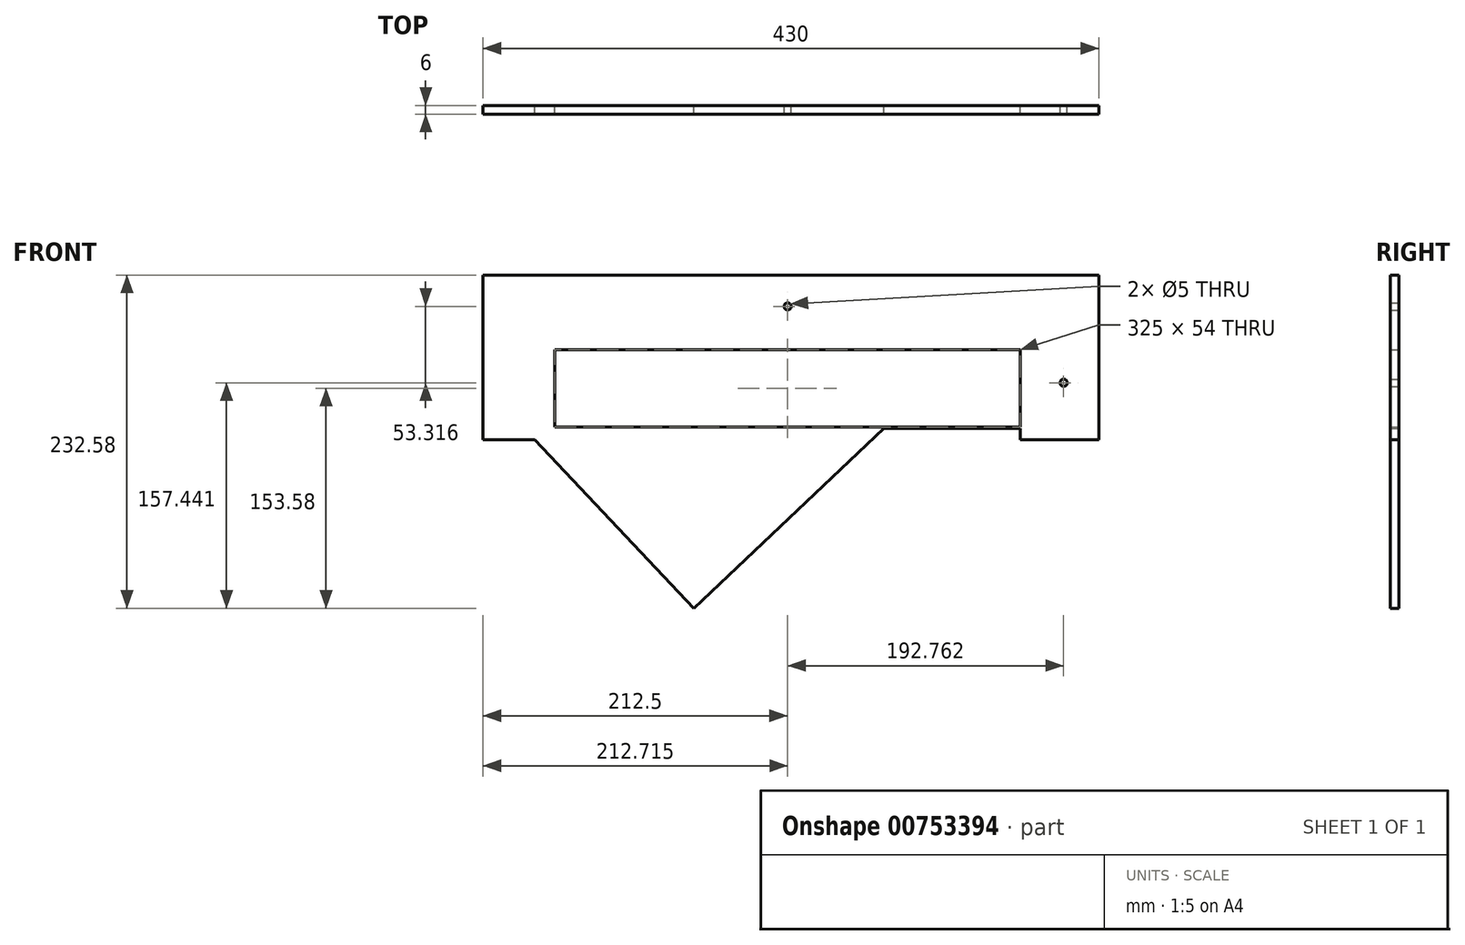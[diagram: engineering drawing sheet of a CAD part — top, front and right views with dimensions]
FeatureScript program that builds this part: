
annotation { "Feature Type Name" : "Feature", "Feature Type Description" : "" }
export const myFeature = defineFeature(function(context is Context, id is Id, definition is map)
    precondition{}
    {
        {
            var Q0;
            Q0=qCreatedBy(makeId("Front.planeOp"),FACE);
            var sketch = newSketch(context, id + "F0", { "sketchPlane" : qUnion([Q0])});
            skLineSegment(sketch, "E0", {"start": v(0, 0) * mm, "end": v(0, 115) * mm});
            skLineSegment(sketch, "E1", {"start": v(0, 115) * mm, "end": v(430, 115) * mm});
            skLineSegment(sketch, "E2", {"start": v(430, 115) * mm, "end": v(430, 0) * mm});
            skLineSegment(sketch, "E3", {"start": v(430, 0) * mm, "end": v(375, 0) * mm});
            skLineSegment(sketch, "E4", {"start": v(375, 0) * mm, "end": v(375, 8) * mm});
            skLineSegment(sketch, "E5", {"start": v(375, 63) * mm, "end": v(50, 63) * mm});
            skLineSegment(sketch, "E6", {"start": v(50, 63) * mm, "end": v(50, 9) * mm});
            skLineSegment(sketch, "E7", {"start": v(50, 0) * mm, "end": v(0, 0) * mm});
            skLineSegment(sketch, "E8", {"start": v(50, 9) * mm, "end": v(375, 9) * mm});
            skLineSegment(sketch, "E9.0", {"start": v(50, 8) * mm, "end": v(375, 8) * mm});
            skLineSegment(sketch, "E10.trimOffspring", {"start": v(50, 8) * mm, "end": v(50, 0) * mm});
            skLineSegment(sketch, "E11.trimOffspring", {"start": v(375, 9) * mm, "end": v(375, 63) * mm});
            skCircle(sketch, "E12", {"center": v(405.48, 39.86) * mm, "radius": 2.5 * mm});
            skCircle(sketch, "E13", {"center": v(212.71, 93.18) * mm, "radius": 2.5 * mm});
            skLineSegment(sketch, "E14", {"start": v(212.71, 93.18) * mm, "end": v(405.48, 39.86) * mm, "construction": true});
            skLineSegment(sketch, "E15", {"start": v(279.89, 8) * mm, "end": v(212.71, 93.18) * mm, "construction": true});
            skLineSegment(sketch, "E16", {"start": v(279.89, 8) * mm, "end": v(147.23, -117.58) * mm});
            skLineSegment(sketch, "E17", {"start": v(147.23, -117.58) * mm, "end": v(14.03, 23.13) * mm});
            skSolve(sketch);
        }
        {
            var Q0;
            {var subQ0=sQuery(id+"F0.wireOp",EDGE,"OpYctbiN-NgkZ-EWBk-AkG0-0JdFd2dzPY2s");var subQ1=sQuery(id+"F0.wireOp",EDGE,"E8");var subQ2=makeQuery(id+"F0.imprint","INTERSECT",VERTEX,{"derivedFrom":[subQ1,subQ0]});Q0=makeQuery(id+"F0.imprint","IMPRINT",FACE,{"disambiguationData":[TD([[makeQuery(id+"F0.imprint","IMPRINT",EDGE,{"disambiguationData":[TD([[subQ2,-1.0]])],"derivedFrom":subQ1}),-1.0]])]});}
            var Q1;
            Q1=makeQuery(id+"F0.imprint","IMPRINT",FACE,{"disambiguationData":[TD([[makeQuery(id+"F0.imprint","IMPRINT",EDGE,{"derivedFrom":sQuery(id+"F0.wireOp",EDGE,"E0")}),-1.0]])]});
            var Q2;
            {var subQ0=sQuery(id+"F0.wireOp",EDGE,"OpYctbiN-NgkZ-EWBk-AkG0-0JdFd2dzPY2s");var subQ1=sQuery(id+"F0.wireOp",EDGE,"E9.0");var subQ2=makeQuery(id+"F0.imprint","INTERSECT",VERTEX,{"derivedFrom":[subQ1,subQ0]});Q2=makeQuery(id+"F0.imprint","IMPRINT",FACE,{"disambiguationData":[TD([[makeQuery(id+"F0.imprint","IMPRINT",EDGE,{"disambiguationData":[TD([[subQ2,-1.0]])],"derivedFrom":subQ1}),-1.0]])]});}
            extrude(context, id + "F1", {"entities" : qUnion([Q0, Q1, Q2]), "depth" : 6 * mm, "offsetDistance" : 25 * mm});
        }
    });
